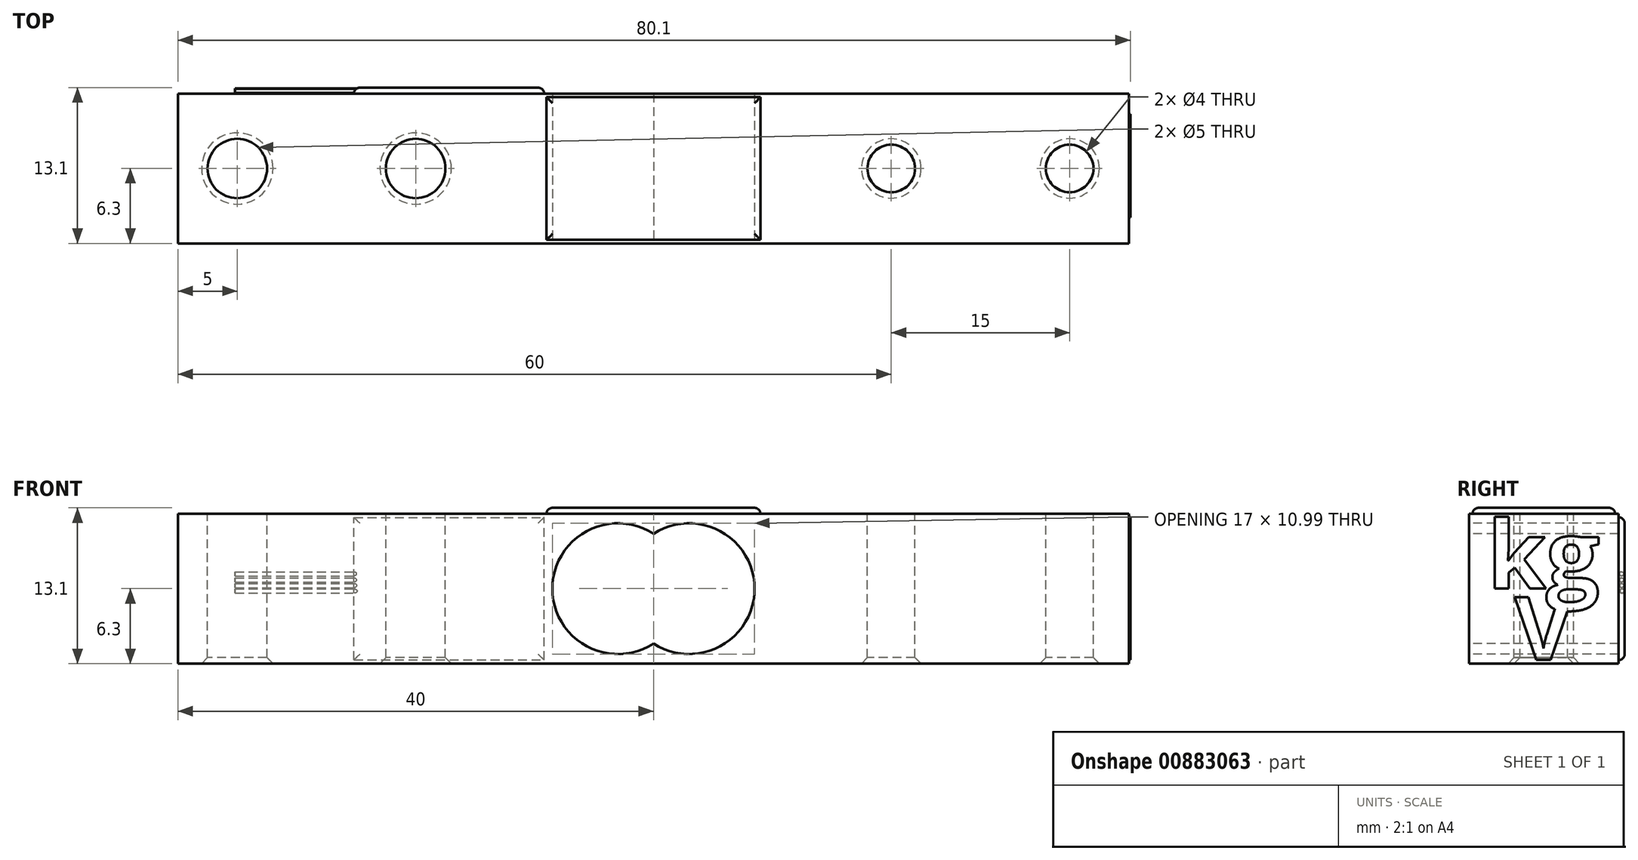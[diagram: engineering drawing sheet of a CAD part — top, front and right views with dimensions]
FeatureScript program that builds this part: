
annotation { "Feature Type Name" : "Feature", "Feature Type Description" : "" }
export const myFeature = defineFeature(function(context is Context, id is Id, definition is map)
    precondition{}
    {
        {
            var Q0;
            Q0=qCreatedBy(makeId("Top.planeOp"),FACE);
            var sketch = newSketch(context, id + "F0", { "sketchPlane" : qUnion([Q0])});
            skLineSegment(sketch, "E0.bottom", {"start": v(40, -6.3) * mm, "end": v(-40, -6.3) * mm});
            skLineSegment(sketch, "E0.top", {"start": v(40, 6.3) * mm, "end": v(-40, 6.3) * mm});
            skLineSegment(sketch, "E0.left", {"start": v(40, -6.3) * mm, "end": v(40, 6.3) * mm});
            skLineSegment(sketch, "E0.right", {"start": v(-40, -6.3) * mm, "end": v(-40, 6.3) * mm});
            skPoint(sketch, "E0.middle", {"position": v(0, 0) * mm});
            skSolve(sketch);
        }
        {
            var Q0;
            Q0=makeQuery(id+"F0.imprint","IMPRINT",FACE,{"disambiguationData":[TD([[makeQuery(id+"F0.imprint","IMPRINT",EDGE,{"derivedFrom":sQuery(id+"F0.wireOp",EDGE,"E0.bottom")}),-1.0]])]});
            extrude(context, id + "F1", {"entities" : qUnion([Q0]), "depth" : 12.6 * mm, "offsetDistance" : 25 * mm});
        }
        {
            var Q0;
            Q0=makeQuery(id+"F1.opExtrude","CAP_FACE",FACE,{"disambiguationData":[OSD([sQuery(id+"F0.wireOp",EDGE,"E0.bottom"),sQuery(id+"F0.wireOp",EDGE,"E0.top"),sQuery(id+"F0.wireOp",EDGE,"E0.left"),sQuery(id+"F0.wireOp",EDGE,"E0.right")])],"isStart":false});
            var sketch = newSketch(context, id + "F2", { "sketchPlane" : qUnion([Q0])});
            skCircle(sketch, "E1", {"center": v(-35, 0) * mm, "radius": 2.5 * mm});
            skCircle(sketch, "E2", {"center": v(-20, 0) * mm, "radius": 2.5 * mm});
            skCircle(sketch, "E3", {"center": v(20, 0) * mm, "radius": 2 * mm});
            skCircle(sketch, "E4", {"center": v(35, 0) * mm, "radius": 2 * mm});
            skSolve(sketch);
        }
        {
            var Q0;
            Q0=qSketchRegion(id+"F2",true);
            extrude(context, id + "F3", {"entities" : qUnion([Q0]), "operationType" : NewBodyOperationType.REMOVE, "endBound" : BoundingType.THROUGH_ALL, "oppositeDirection" : true, "depth" : 25 * mm, "offsetDistance" : 25 * mm});
        }
        {
            var Q0;
            Q0=makeQuery(id+"F1.opExtrude","SWEPT_FACE",FACE,{"disambiguationData":[OSD([sQuery(id+"F0.wireOp",EDGE,"E0.bottom")])]});
            var sketch = newSketch(context, id + "F4", { "sketchPlane" : qUnion([Q0])});
            skLineSegment(sketch, "E5", {"start": v(0, 0) * mm, "end": v(0, 12.6) * mm, "construction": true});
            skLineSegment(sketch, "E6", {"start": v(-6.4, 6.3) * mm, "end": v(0, 6.3) * mm, "construction": true});
            skPoint(sketch, "E6.endSnap0", {"position": v(0, 6.3) * mm});
            skCircle(sketch, "E7", {"center": v(-3, 6.3) * mm, "radius": 5.5 * mm});
            skCircle(sketch, "E8", {"center": v(3, 6.3) * mm, "radius": 5.5 * mm});
            skSolve(sketch);
        }
        {
            var Q0;
            Q0=qSketchRegion(id+"F4",true);
            extrude(context, id + "F5", {"entities" : qUnion([Q0]), "operationType" : NewBodyOperationType.REMOVE, "endBound" : BoundingType.THROUGH_ALL, "oppositeDirection" : true, "depth" : 25 * mm, "offsetDistance" : 25 * mm});
        }
        {
            var Q0;
            Q0=makeQuery(id+"F1.opExtrude","SWEPT_FACE",FACE,{"disambiguationData":[OSD([sQuery(id+"F0.wireOp",EDGE,"E0.left")])]});
            var sketch = newSketch(context, id + "F6", { "sketchPlane" : qUnion([Q0])});
            skText(sketch, "E9", { "text": "V", "fontName": "OpenSans-Bold.ttf"});
            skText(sketch, "E10", { "text": "kg", "fontName": "OpenSans-Bold.ttf"});
            skPoint(sketch, "E10.secondSnap0", {"position": v(6.3, 6.3) * mm});
            const initialGuessF6  = {"E9": [-0.00244, 0.0003, 1, 0, 0.00534], "E10": [-0.00475, 0.0063, 1, 0, 0.00573]};
            skSetInitialGuess(sketch, initialGuessF6);
            skSolve(sketch);
        }
        {
            var Q0;
            Q0=qSketchRegion(id+"F6",true);
            extrude(context, id + "F7", {"entities" : qUnion([Q0]), "operationType" : NewBodyOperationType.ADD, "depth" : 0.1 * mm, "offsetDistance" : 25 * mm});
        }
        {
            var Q0;
            Q0=makeQuery(id+"F1.opExtrude","CAP_FACE",FACE,{"disambiguationData":[OSD([sQuery(id+"F0.wireOp",EDGE,"E0.bottom"),sQuery(id+"F0.wireOp",EDGE,"E0.top"),sQuery(id+"F0.wireOp",EDGE,"E0.left"),sQuery(id+"F0.wireOp",EDGE,"E0.right")])],"isStart":false});
            var sketch = newSketch(context, id + "F8", { "sketchPlane" : qUnion([Q0])});
            skLineSegment(sketch, "E11.bottom", {"start": v(-9, -6) * mm, "end": v(9, -6) * mm});
            skLineSegment(sketch, "E11.top", {"start": v(-9, 6) * mm, "end": v(9, 6) * mm});
            skLineSegment(sketch, "E11.left", {"start": v(-9, -6) * mm, "end": v(-9, 6) * mm});
            skLineSegment(sketch, "E11.right", {"start": v(9, -6) * mm, "end": v(9, 6) * mm});
            skPoint(sketch, "E11.middle", {"position": v(0, 0) * mm});
            skSolve(sketch);
        }
        {
            var Q0;
            Q0=makeQuery(id+"F8.imprint","IMPRINT",FACE,{"disambiguationData":[TD([[makeQuery(id+"F8.imprint","IMPRINT",EDGE,{"derivedFrom":sQuery(id+"F8.wireOp",EDGE,"E11.bottom")}),1.0]])]});
            extrude(context, id + "F9", {"entities" : qUnion([Q0]), "operationType" : NewBodyOperationType.ADD, "depth" : 0.5 * mm, "offsetDistance" : 25 * mm});
        }
        {
            var Q0;
            Q0=makeQuery(id+"F1.opExtrude","SWEPT_FACE",FACE,{"disambiguationData":[OSD([sQuery(id+"F0.wireOp",EDGE,"E0.top")])]});
            var sketch = newSketch(context, id + "F10", { "sketchPlane" : qUnion([Q0])});
            skLineSegment(sketch, "E12.bottom", {"start": v(25.2, 0.3) * mm, "end": v(9.2, 0.3) * mm});
            skLineSegment(sketch, "E12.top", {"start": v(25.2, 12.3) * mm, "end": v(9.2, 12.3) * mm});
            skLineSegment(sketch, "E12.left", {"start": v(25.2, 0.3) * mm, "end": v(25.2, 12.3) * mm});
            skLineSegment(sketch, "E12.right", {"start": v(9.2, 0.3) * mm, "end": v(9.2, 12.3) * mm});
            skPoint(sketch, "E12.middle", {"position": v(17.2, 6.3) * mm});
            skLineSegment(sketch, "E13", {"start": v(40, 6.3) * mm, "end": v(-39.38, 6.3) * mm, "construction": true});
            skSolve(sketch);
        }
        {
            var Q0;
            Q0=makeQuery(id+"F10.imprint","IMPRINT",FACE,{"disambiguationData":[TD([[makeQuery(id+"F10.imprint","IMPRINT",EDGE,{"derivedFrom":sQuery(id+"F10.wireOp",EDGE,"E12.bottom")}),-1.0]])]});
            extrude(context, id + "F11", {"entities" : qUnion([Q0]), "operationType" : NewBodyOperationType.ADD, "depth" : 0.5 * mm, "offsetDistance" : 25 * mm});
        }
        {
            var Q0;
            Q0=makeQuery(id+"F11.opExtrude","SWEPT_FACE",FACE,{"disambiguationData":[OSD([sQuery(id+"F10.wireOp",EDGE,"E12.left")])]});
            var sketch = newSketch(context, id + "F12", { "sketchPlane" : qUnion([Q0])});
            skCircle(sketch, "E14", {"center": v(-6.53, 7.55) * mm, "radius": 0.17 * mm});
            skCircle(sketch, "E15", {"center": v(-6.54, 7.03) * mm, "radius": 0.17 * mm});
            skCircle(sketch, "E16", {"center": v(-6.55, 6.57) * mm, "radius": 0.17 * mm});
            skCircle(sketch, "E17", {"center": v(-6.57, 6.1) * mm, "radius": 0.17 * mm});
            skSolve(sketch);
        }
        {
            var Q0;
            Q0=qSketchRegion(id+"F12",true);
            extrude(context, id + "F13", {"entities" : qUnion([Q0]), "operationType" : NewBodyOperationType.ADD, "depth" : 10 * mm, "offsetDistance" : 25 * mm});
        }
        {
            var Q0;
            Q0=makeQuery(id+"F9.opExtrude","CAP_FACE",FACE,{"disambiguationData":[OSD([sQuery(id+"F8.wireOp",EDGE,"E11.bottom"),sQuery(id+"F8.wireOp",EDGE,"E11.top"),sQuery(id+"F8.wireOp",EDGE,"E11.left"),sQuery(id+"F8.wireOp",EDGE,"E11.right")])],"isStart":false});
            var Q1;
            Q1=makeQuery(id+"F11.opExtrude","CAP_FACE",FACE,{"disambiguationData":[OSD([sQuery(id+"F10.wireOp",EDGE,"E12.bottom"),sQuery(id+"F10.wireOp",EDGE,"E12.top"),sQuery(id+"F10.wireOp",EDGE,"E12.left"),sQuery(id+"F10.wireOp",EDGE,"E12.right")])],"isStart":false});
            fillet(context, id + "F14", {"entities" : qUnion([Q0, Q1]), "radius" : 0.5 * mm, "tangentPropagation" : true, "allowEdgeOverflow" : false});
        }
        {
            var Q0;
            Q0=makeQuery(id+"F3.boolean.opBoolean","COPY",EDGE,{"derivedFrom":makeQuery(id+"F3.opExtrude","CAP_EDGE",EDGE,{"disambiguationData":[OSD([sQuery(id+"F2.wireOp",EDGE,"E2")])],"isStart":true})});
            var Q1;
            Q1=makeQuery(id+"F3.boolean.opBoolean","COPY",EDGE,{"derivedFrom":makeQuery(id+"F3.opExtrude","CAP_EDGE",EDGE,{"disambiguationData":[OSD([sQuery(id+"F2.wireOp",EDGE,"E1")])],"isStart":true})});
            var Q2;
            Q2=makeQuery(id+"F3.boolean.opBoolean","COPY",EDGE,{"derivedFrom":makeQuery(id+"F3.opExtrude","CAP_EDGE",EDGE,{"disambiguationData":[OSD([sQuery(id+"F2.wireOp",EDGE,"E3")])],"isStart":true})});
            var Q3;
            Q3=makeQuery(id+"F3.boolean.opBoolean","COPY",EDGE,{"derivedFrom":makeQuery(id+"F3.opExtrude","CAP_EDGE",EDGE,{"disambiguationData":[OSD([sQuery(id+"F2.wireOp",EDGE,"E4")])],"isStart":true})});
            var Q4;
            Q4=makeQuery(id+"F3.boolean.opBoolean","INTERSECT",EDGE,{"derivedFrom":[makeQuery(id+"F1.opExtrude","CAP_FACE",FACE,{"disambiguationData":[OSD([sQuery(id+"F0.wireOp",EDGE,"E0.bottom"),sQuery(id+"F0.wireOp",EDGE,"E0.top"),sQuery(id+"F0.wireOp",EDGE,"E0.left"),sQuery(id+"F0.wireOp",EDGE,"E0.right")])],"isStart":true}),makeQuery(id+"F3.opExtrude","SWEPT_FACE",FACE,{"disambiguationData":[OSD([sQuery(id+"F2.wireOp",EDGE,"E4")])]})]});
            var Q5;
            Q5=makeQuery(id+"F3.boolean.opBoolean","INTERSECT",EDGE,{"derivedFrom":[makeQuery(id+"F1.opExtrude","CAP_FACE",FACE,{"disambiguationData":[OSD([sQuery(id+"F0.wireOp",EDGE,"E0.bottom"),sQuery(id+"F0.wireOp",EDGE,"E0.top"),sQuery(id+"F0.wireOp",EDGE,"E0.left"),sQuery(id+"F0.wireOp",EDGE,"E0.right")])],"isStart":true}),makeQuery(id+"F3.opExtrude","SWEPT_FACE",FACE,{"disambiguationData":[OSD([sQuery(id+"F2.wireOp",EDGE,"E3")])]})]});
            var Q6;
            Q6=makeQuery(id+"F3.boolean.opBoolean","INTERSECT",EDGE,{"derivedFrom":[makeQuery(id+"F1.opExtrude","CAP_FACE",FACE,{"disambiguationData":[OSD([sQuery(id+"F0.wireOp",EDGE,"E0.bottom"),sQuery(id+"F0.wireOp",EDGE,"E0.top"),sQuery(id+"F0.wireOp",EDGE,"E0.left"),sQuery(id+"F0.wireOp",EDGE,"E0.right")])],"isStart":true}),makeQuery(id+"F3.opExtrude","SWEPT_FACE",FACE,{"disambiguationData":[OSD([sQuery(id+"F2.wireOp",EDGE,"E2")])]})]});
            var Q7;
            Q7=makeQuery(id+"F3.boolean.opBoolean","INTERSECT",EDGE,{"derivedFrom":[makeQuery(id+"F1.opExtrude","CAP_FACE",FACE,{"disambiguationData":[OSD([sQuery(id+"F0.wireOp",EDGE,"E0.bottom"),sQuery(id+"F0.wireOp",EDGE,"E0.top"),sQuery(id+"F0.wireOp",EDGE,"E0.left"),sQuery(id+"F0.wireOp",EDGE,"E0.right")])],"isStart":true}),makeQuery(id+"F3.opExtrude","SWEPT_FACE",FACE,{"disambiguationData":[OSD([sQuery(id+"F2.wireOp",EDGE,"E1")])]})]});
            chamfer(context, id + "F15", {"entities" : qUnion([Q0, Q1, Q2, Q3, Q4, Q5, Q6, Q7]), "width" : 0.5 * mm, "tangentPropagation" : true});
        }
    });
